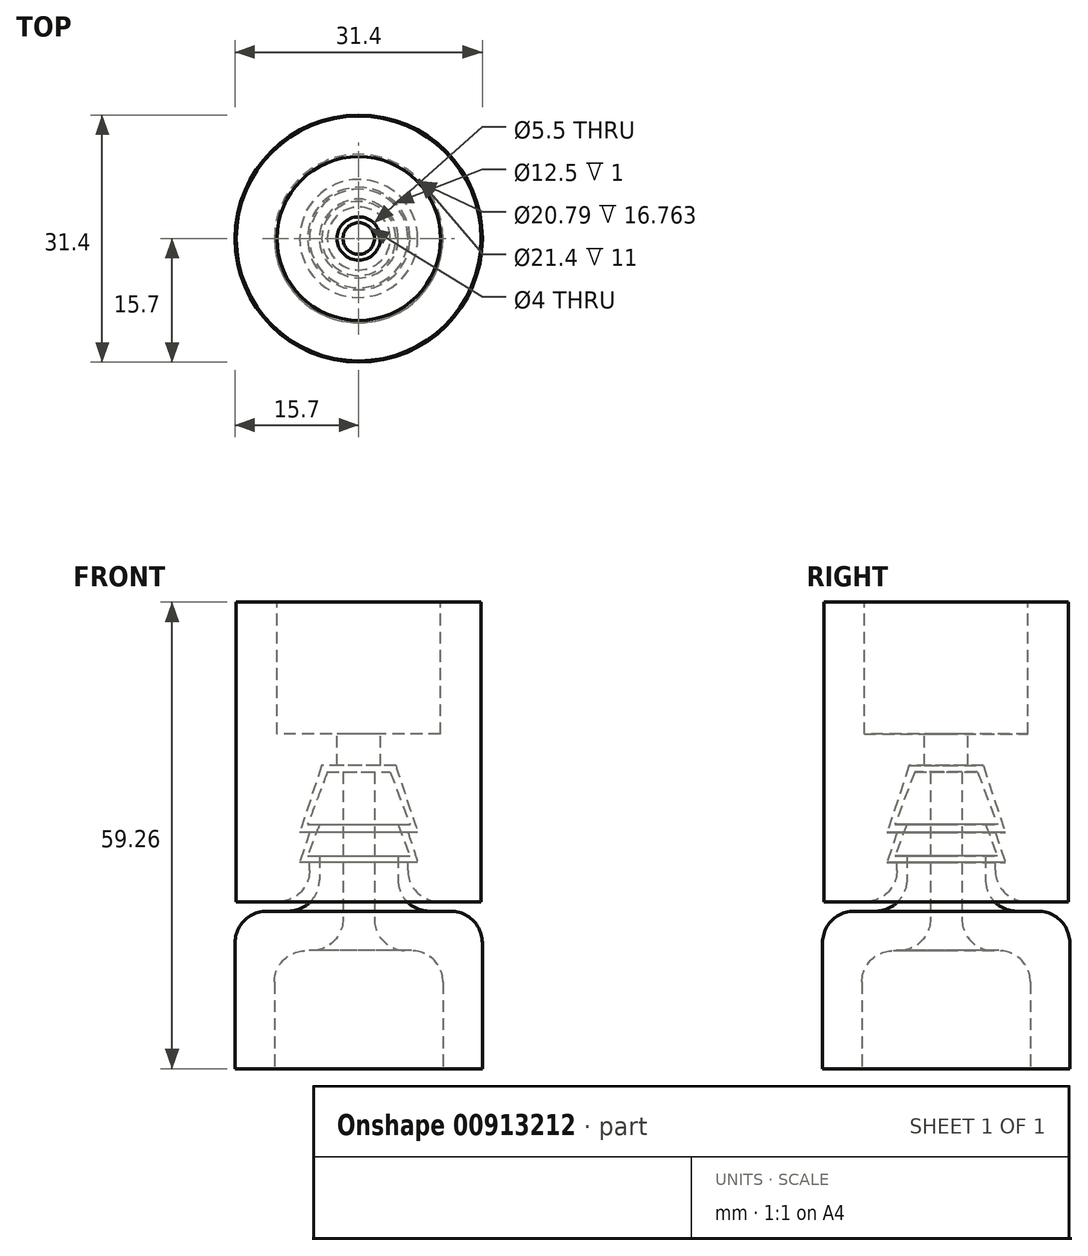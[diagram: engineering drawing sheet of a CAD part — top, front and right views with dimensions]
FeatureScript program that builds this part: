
annotation { "Feature Type Name" : "Feature", "Feature Type Description" : "" }
export const myFeature = defineFeature(function(context is Context, id is Id, definition is map)
    precondition{}
    {
        {
            var Q0;
            Q0=qCreatedBy(makeId("Front.planeOp"),FACE);
            var sketch = newSketch(context, id + "F0", { "sketchPlane" : qUnion([Q0])});
            skLineSegment(sketch, "E0", {"start": v(10.7, -15) * mm, "end": v(10.7, 0) * mm});
            skLineSegment(sketch, "E1", {"start": v(10.7, 0) * mm, "end": v(2, 0) * mm});
            skLineSegment(sketch, "E2", {"start": v(2, 0) * mm, "end": v(2, 22.67) * mm});
            skLineSegment(sketch, "E3", {"start": v(2, 22.67) * mm, "end": v(4, 22.67) * mm});
            skLineSegment(sketch, "E4", {"start": v(4, 22.67) * mm, "end": v(6.5, 16) * mm});
            skLineSegment(sketch, "E5", {"start": v(6.5, 16) * mm, "end": v(5, 16) * mm});
            skLineSegment(sketch, "E6", {"start": v(5, 16) * mm, "end": v(6.5, 12) * mm});
            skLineSegment(sketch, "E7", {"start": v(6.5, 12) * mm, "end": v(5, 12) * mm});
            skLineSegment(sketch, "E8", {"start": v(5, 12) * mm, "end": v(5, 5) * mm});
            skLineSegment(sketch, "E9", {"start": v(5, 5) * mm, "end": v(15.7, 5) * mm});
            skLineSegment(sketch, "E10", {"start": v(15.7, 5) * mm, "end": v(15.7, -15) * mm});
            skLineSegment(sketch, "E11", {"start": v(15.7, -15) * mm, "end": v(10.7, -15) * mm});
            skLineSegment(sketch, "E12", {"start": v(0, 0) * mm, "end": v(0, 39.05) * mm, "construction": true});
            skSolve(sketch);
        }
        {
            var Q0;
            Q0=makeQuery(id+"F0.imprint","IMPRINT",FACE,{"disambiguationData":[TD([[makeQuery(id+"F0.imprint","IMPRINT",EDGE,{"derivedFrom":sQuery(id+"F0.wireOp",EDGE,"E0")}),-1.0]])]});
            var Q1;
            Q1=sQuery(id+"F0.wireOp",EDGE,"E12");
            var Q2;
            Q2=sQuery(id+"F0.wireOp",EDGE,"E12");
            revolve(context, id + "F1", {"surfaceOperationType" : NewSurfaceOperationType.NEW, "entities" : qUnion([Q0]), "surfaceEntities" : qUnion([Q1]), "axis" : qUnion([Q2]), "revolveType" : RevolveType.FULL});
        }
        {
            var Q0;
            Q0=makeQuery(id+"F1.opRevolve","SWEPT_EDGE",EDGE,{"disambiguationData":[OSD([sQuery(id+"F0.wireOp",EDGE,"E8"),sQuery(id+"F0.wireOp",EDGE,"E9")])]});
            var Q1;
            Q1=makeQuery(id+"F1.opRevolve","SWEPT_EDGE",EDGE,{"disambiguationData":[OSD([sQuery(id+"F0.wireOp",EDGE,"E9"),sQuery(id+"F0.wireOp",EDGE,"E10")])]});
            var Q2;
            Q2=makeQuery(id+"F1.opRevolve","SWEPT_EDGE",EDGE,{"disambiguationData":[OSD([sQuery(id+"F0.wireOp",EDGE,"E0"),sQuery(id+"F0.wireOp",EDGE,"E1")])]});
            var Q3;
            Q3=makeQuery(id+"F1.opRevolve","SWEPT_EDGE",EDGE,{"disambiguationData":[OSD([sQuery(id+"F0.wireOp",EDGE,"E1"),sQuery(id+"F0.wireOp",EDGE,"E2")])]});
            fillet(context, id + "F2", {"entities" : qUnion([Q0, Q1, Q2, Q3]), "radius" : 4 * mm, "tangentPropagation" : true, "allowEdgeOverflow" : false});
        }
        {
            var Q0;
            Q0=qCreatedBy(makeId("Front.planeOp"),FACE);
            var sketch = newSketch(context, id + "F3", { "sketchPlane" : qUnion([Q0])});
            skLineSegment(sketch, "E13", {"start": v(0, 36.58) * mm, "end": v(0, 0) * mm, "construction": true});
            skLineSegment(sketch, "E14", {"start": v(2.75, 23.5) * mm, "end": v(4.71, 23.5) * mm});
            skLineSegment(sketch, "E15", {"start": v(4.71, 23.5) * mm, "end": v(7.5, 15.01) * mm});
            skLineSegment(sketch, "E16", {"start": v(7.5, 15.01) * mm, "end": v(6.25, 15.01) * mm});
            skLineSegment(sketch, "E17", {"start": v(6.25, 15.01) * mm, "end": v(7.5, 11.21) * mm});
            skLineSegment(sketch, "E18", {"start": v(7.5, 11.21) * mm, "end": v(6.25, 11.21) * mm});
            skLineSegment(sketch, "E19", {"start": v(6.25, 11.21) * mm, "end": v(6.25, 6.21) * mm});
            skLineSegment(sketch, "E20", {"start": v(6.25, 6.21) * mm, "end": v(15.55, 6.21) * mm});
            skLineSegment(sketch, "E21", {"start": v(15.55, 6.21) * mm, "end": v(15.55, 44.26) * mm});
            skLineSegment(sketch, "E22", {"start": v(15.55, 44.26) * mm, "end": v(10.4, 44.26) * mm});
            skLineSegment(sketch, "E23", {"start": v(10.4, 44.26) * mm, "end": v(10.4, 27.5) * mm});
            skLineSegment(sketch, "E24", {"start": v(10.4, 27.5) * mm, "end": v(2.75, 27.5) * mm});
            skLineSegment(sketch, "E25", {"start": v(2.75, 27.5) * mm, "end": v(2.75, 23.5) * mm});
            skLineSegment(sketch, "E26.MirrorCS", {"start": v(-10.4, 44.26) * mm, "end": v(-10.4, 27.5) * mm});
            skLineSegment(sketch, "E27.MirrorCS", {"start": v(-15.55, 6.21) * mm, "end": v(-15.55, 44.26) * mm});
            skLineSegment(sketch, "E28.MirrorCS", {"start": v(-15.55, 44.26) * mm, "end": v(-10.4, 44.26) * mm});
            skLineSegment(sketch, "E29.MirrorCS", {"start": v(-10.4, 27.5) * mm, "end": v(-2.75, 27.5) * mm});
            skLineSegment(sketch, "E30.MirrorCS", {"start": v(-6.25, 6.21) * mm, "end": v(-15.55, 6.21) * mm});
            skLineSegment(sketch, "E31.MirrorCS", {"start": v(-4.71, 23.5) * mm, "end": v(-7.5, 15.01) * mm});
            skLineSegment(sketch, "E32.MirrorCS", {"start": v(-6.25, 15.01) * mm, "end": v(-7.5, 11.21) * mm});
            skLineSegment(sketch, "E33.MirrorCS", {"start": v(-2.75, 27.5) * mm, "end": v(-2.75, 23.5) * mm});
            skLineSegment(sketch, "E34.MirrorCS", {"start": v(-6.25, 11.21) * mm, "end": v(-6.25, 6.21) * mm});
            skSolve(sketch);
        }
        {
            var Q0;
            Q0=makeQuery(id+"F3.imprint","IMPRINT",FACE,{"disambiguationData":[TD([[makeQuery(id+"F3.imprint","IMPRINT",EDGE,{"derivedFrom":sQuery(id+"F3.wireOp",EDGE,"E14")}),1.0]])]});
            var Q1;
            Q1=sQuery(id+"F3.wireOp",EDGE,"E13");
            revolve(context, id + "F4", {"surfaceOperationType" : NewSurfaceOperationType.NEW, "entities" : qUnion([Q0]), "axis" : qUnion([Q1]), "revolveType" : RevolveType.FULL});
        }
        {
            var Q0;
            Q0=makeQuery(id+"F4.opRevolve","SWEPT_EDGE",EDGE,{"disambiguationData":[OSD([sQuery(id+"F3.wireOp",EDGE,"E19"),sQuery(id+"F3.wireOp",EDGE,"E20")])]});
            fillet(context, id + "F5", {"entities" : qUnion([Q0]), "radius" : 4 * mm, "tangentPropagation" : true, "allowEdgeOverflow" : false});
        }
    });
